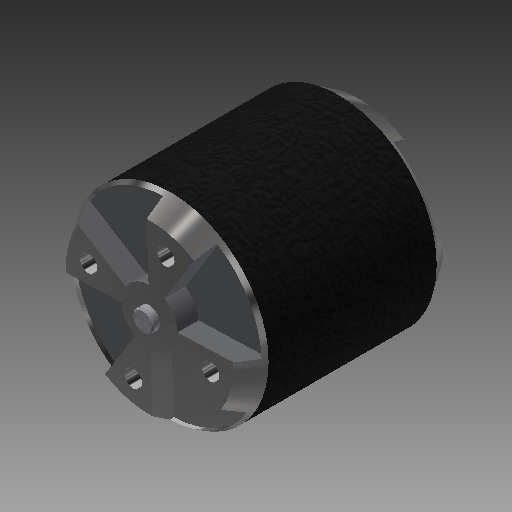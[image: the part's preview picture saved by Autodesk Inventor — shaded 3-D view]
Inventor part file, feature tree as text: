
AUTODESK INVENTOR PART (.ipt)
format: ipt  version: 2019 (Build 230136000, 136)  size: 302,080 bytes
history: native  units: mm
features: sketch x9, extrude x7, pattern_circular x4, chamfer x3, projected_geometry x3, other x2, hole x1, plane x1
ambient origin geometry x8: Origin, YZ Plane, XZ Plane, XY Plane, X Axis, Y Axis, Z Axis, Center Point
bodies: Solid1 (feature_tree)
feature tree (30):
  extrude  "Extrusion1"  Depth=30.0mm TaperAngle=0.0deg
  chamfer  "Chamfer1"  Distance=2.0mm Angle=45.0deg
  chamfer  "Chamfer2"  Distance=2.0mm Angle=45.0deg
  extrude  "Extrusion2"  Depth=1.4mm TaperAngle=0.0deg
  extrude  "Extrusion3"  Depth=16.0mm
  pattern_circular  "Circular Pattern1"  Count=3 Angle=360.0deg
  hole  "Hole1"  [1 undecoded]
  pattern_circular  "Circular Pattern2"  Count=4 Angle=360.0deg
  extrude  "Extrusion4"  Depth=1.0mm TaperAngle=0.0deg
  extrude  "Extrusion5"  Depth=2.0mm TaperAngle=45.0deg
  pattern_circular  "Circular Pattern3"  [2 undecoded]
  extrude  "Extrusion6"  Depth=5.0mm
  chamfer  "Chamfer3"  Distance=5.0mm
  extrude  "Extrusion7"  Depth=5.0mm TaperAngle=360.0deg
  pattern_circular  "Circular Pattern4"  [2 undecoded]
  plane  "Work Plane1"
  other  "Decal1"
  sketch  "Sketch1"  dims[d0=28.0mm d1=30.0mm d2=0.0mm d3=2.0mm d4=3.0mm d5=45.0deg d6=2.0mm d7=3.0mm d8=45.0deg]
  sketch  "Sketch2"  dims[d9=8.0mm d10=1.4mm d11=0.0mm]
  sketch  "Sketch3"  dims[d12=4.886922mm d13=16.0mm]
  sketch  "Sketch4"  dims[d14=2.4mm d15=0.0mm d16=30.0mm d17=360.0deg]
  sketch  "Sketch6"  dims[d19=8.0mm]
  projected_geometry  "Projected Loop1"
  projected_geometry  "Projected Loop2"
  sketch  "Sketch7"  dims[d20=2.013mm d21=4.0mm d22=4.0mm d23=2.0mm d24=90.0deg d25=4.0mm d26=20.594885mm d27=30.0mm d28=360.0deg]
  projected_geometry  "Projected Loop3"
  sketch  "Sketch8"  dims[d30=10.0mm d31=0.0mm]
  sketch  "Sketch9"  dims[d32=3.0mm d33=0.0mm d34=40.0mm d35=360.0deg]
  sketch  "Sketch10"  dims[d37=3.0mm d38=1.0mm d39=0.0mm d40=0.2mm d41=2.0mm d42=45.0deg d43=2.5mm d44=9.0mm d45=5.0mm d46=0.0mm d47=40.0mm d48=360.0deg]
  other  "Image2"
note: 5 required parameter values undecoded (feature->parameter linkage not recoverable at this tier; creation-order binding heuristic only, values carry confidence <= 0.55)
